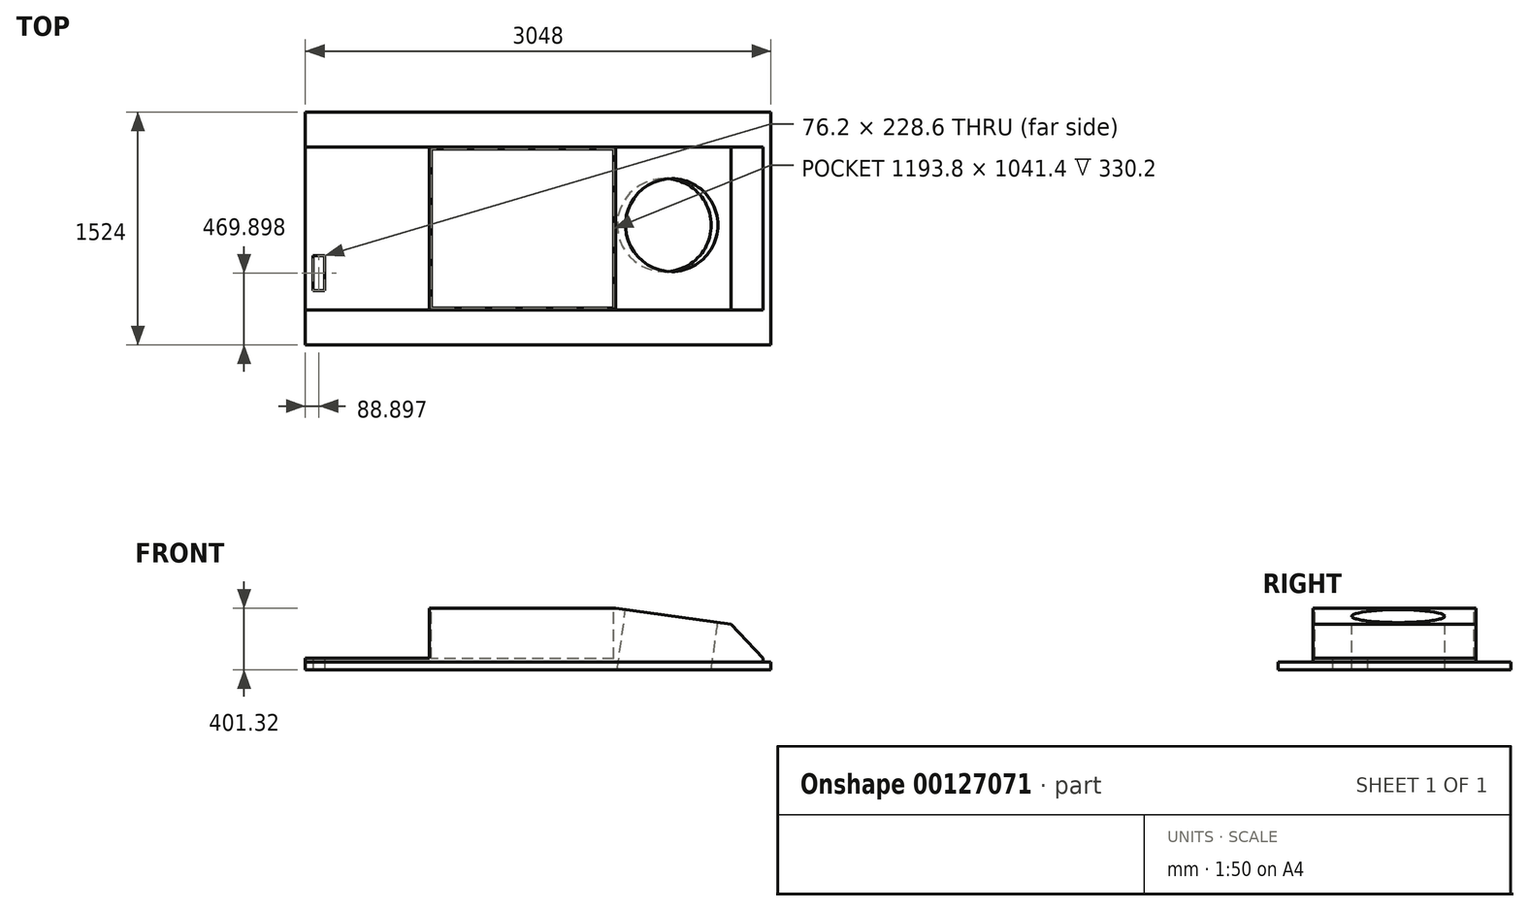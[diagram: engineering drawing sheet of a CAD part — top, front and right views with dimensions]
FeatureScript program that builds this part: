
annotation { "Feature Type Name" : "Feature", "Feature Type Description" : "" }
export const myFeature = defineFeature(function(context is Context, id is Id, definition is map)
    precondition{}
    {
        {
            var Q0;
            Q0=qCreatedBy(makeId("Top.planeOp"),FACE);
            var sketch = newSketch(context, id + "F0", { "sketchPlane" : qUnion([Q0])});
            skLineSegment(sketch, "E0.bottom", {"start": v(-1508.2, 739.4) * mm, "end": v(1539.8, 739.4) * mm});
            skLineSegment(sketch, "E0.top", {"start": v(-1508.2, -784.6) * mm, "end": v(1539.8, -784.6) * mm});
            skLineSegment(sketch, "E0.left", {"start": v(-1508.2, 739.4) * mm, "end": v(-1508.2, -784.6) * mm});
            skLineSegment(sketch, "E0.right", {"start": v(1539.8, 739.4) * mm, "end": v(1539.8, -784.6) * mm});
            skLineSegment(sketch, "E1.bottom", {"start": v(-1381.2, -429) * mm, "end": v(-1457.4, -429) * mm});
            skLineSegment(sketch, "E1.top", {"start": v(-1381.2, -200.4) * mm, "end": v(-1457.4, -200.4) * mm});
            skLineSegment(sketch, "E1.left", {"start": v(-1381.2, -429) * mm, "end": v(-1381.2, -200.4) * mm});
            skLineSegment(sketch, "E1.right", {"start": v(-1457.4, -429) * mm, "end": v(-1457.4, -200.4) * mm});
            skSolve(sketch);
        }
        {
            var Q0;
            Q0=makeQuery(id+"F0.imprint","IMPRINT",FACE,{"disambiguationData":[TD([[makeQuery(id+"F0.imprint","IMPRINT",EDGE,{"derivedFrom":sQuery(id+"F0.wireOp",EDGE,"E0.bottom")}),-1.0]])]});
            extrude(context, id + "F1", {"entities" : qUnion([Q0]), "depth" : 50.8 * mm});
        }
        {
            var Q0;
            Q0=makeQuery(id+"F1.opExtrude","CAP_FACE",FACE,{"disambiguationData":[OSD([sQuery(id+"F0.wireOp",EDGE,"E0.bottom"),sQuery(id+"F0.wireOp",EDGE,"E0.top"),sQuery(id+"F0.wireOp",EDGE,"E0.left"),sQuery(id+"F0.wireOp",EDGE,"E0.right"),sQuery(id+"F0.wireOp",EDGE,"E1.bottom"),sQuery(id+"F0.wireOp",EDGE,"E1.top"),sQuery(id+"F0.wireOp",EDGE,"E1.left"),sQuery(id+"F0.wireOp",EDGE,"E1.right")])],"isStart":false});
            var sketch = newSketch(context, id + "F2", { "sketchPlane" : qUnion([Q0])});
            skLineSegment(sketch, "E2.bottom", {"start": v(-1508.2, -556) * mm, "end": v(1489, -556) * mm});
            skLineSegment(sketch, "E2.top", {"start": v(-1508.2, 510.8) * mm, "end": v(1489, 510.8) * mm});
            skLineSegment(sketch, "E2.left", {"start": v(-1508.2, -556) * mm, "end": v(-1508.2, 510.8) * mm});
            skLineSegment(sketch, "E2.right", {"start": v(1489, -556) * mm, "end": v(1489, 510.8) * mm});
            skSolve(sketch);
        }
        {
            var Q0;
            Q0=makeQuery(id+"F2.imprint","IMPRINT",FACE,{"disambiguationData":[TD([[makeQuery(id+"F2.imprint","IMPRINT",EDGE,{"derivedFrom":sQuery(id+"F2.wireOp",EDGE,"E2.bottom")}),1.0]])]});
            extrude(context, id + "F3", {"entities" : qUnion([Q0]), "operationType" : NewBodyOperationType.ADD, "depth" : 25.4 * mm});
        }
        {
            var Q0;
            Q0=makeQuery(id+"F3.opExtrude","SWEPT_FACE",FACE,{"disambiguationData":[OSD([sQuery(id+"F2.wireOp",EDGE,"E2.top")])]});
            var sketch = newSketch(context, id + "F4", { "sketchPlane" : qUnion([Q0])});
            skLineSegment(sketch, "E3", {"start": v(-1489, 76.2) * mm, "end": v(-1278.6, 296.72) * mm});
            skLineSegment(sketch, "E4", {"start": v(-1278.6, 296.72) * mm, "end": v(-523.8, 401.32) * mm});
            skLineSegment(sketch, "E5", {"start": v(-523.8, 401.32) * mm, "end": v(695.4, 401.32) * mm});
            skLineSegment(sketch, "E6", {"start": v(695.4, 401.32) * mm, "end": v(695.4, 76.2) * mm});
            skLineSegment(sketch, "E7", {"start": v(695.4, 76.2) * mm, "end": v(-1489, 76.2) * mm});
            skSolve(sketch);
        }
        {
            var Q0;
            Q0=makeQuery(id+"F4.imprint","IMPRINT",FACE,{"disambiguationData":[TD([[makeQuery(id+"F4.imprint","IMPRINT",EDGE,{"derivedFrom":sQuery(id+"F4.wireOp",EDGE,"E3")}),-1.0]])]});
            extrude(context, id + "F5", {"entities" : qUnion([Q0]), "operationType" : NewBodyOperationType.ADD, "oppositeDirection" : true, "depth" : 1066.8 * mm});
        }
        {
            var Q0;
            Q0=makeQuery(id+"F5.opExtrude","SWEPT_FACE",FACE,{"disambiguationData":[OSD([sQuery(id+"F4.wireOp",EDGE,"E4")])]});
            var sketch = newSketch(context, id + "F6", { "sketchPlane" : qUnion([Q0])});
            skCircle(sketch, "E8", {"center": v(833.9, 0) * mm, "radius": 304.8 * mm});
            skSolve(sketch);
        }
        {
            var Q0;
            Q0 = qSketchRegion(id + "F6", true);
            extrude(context, id + "F7", {"entities" : qUnion([Q0]), "operationType" : NewBodyOperationType.REMOVE, "endBound" : BoundingType.THROUGH_ALL, "oppositeDirection" : true, "depth" : 682.47 * mm});
        }
        {
            var Q0;
            Q0=makeQuery(id+"F5.opExtrude","SWEPT_FACE",FACE,{"disambiguationData":[OSD([sQuery(id+"F4.wireOp",EDGE,"E5")])]});
            var sketch = newSketch(context, id + "F8", { "sketchPlane" : qUnion([Q0])});
            skLineSegment(sketch, "E9.0", {"start": v(511.1, -543.3) * mm, "end": v(-682.7, -543.3) * mm});
            skLineSegment(sketch, "E10.0", {"start": v(511.1, -543.3) * mm, "end": v(511.1, 498.1) * mm});
            skLineSegment(sketch, "E11.0", {"start": v(511.1, 498.1) * mm, "end": v(-682.7, 498.1) * mm});
            skLineSegment(sketch, "E12.0", {"start": v(-682.7, -543.3) * mm, "end": v(-682.7, 498.1) * mm});
            skSolve(sketch);
        }
        {
            var Q0;
            Q0 = qSketchRegion(id + "F8", true);
            var Q1;
            Q1=makeQuery(id+"F1.opExtrude","SWEPT_BODY",BODY,{"disambiguationData":[OSD([sQuery(id+"F0.wireOp",EDGE,"E0.bottom"),sQuery(id+"F0.wireOp",EDGE,"E0.top"),sQuery(id+"F0.wireOp",EDGE,"E0.left"),sQuery(id+"F0.wireOp",EDGE,"E0.right"),sQuery(id+"F0.wireOp",EDGE,"E1.bottom"),sQuery(id+"F0.wireOp",EDGE,"E1.top"),sQuery(id+"F0.wireOp",EDGE,"E1.left"),sQuery(id+"F0.wireOp",EDGE,"E1.right")])]});
            extrude(context, id + "F9", {"entities" : qUnion([Q0]), "operationType" : NewBodyOperationType.REMOVE, "oppositeDirection" : true, "endBoundEntityBody" : qUnion([Q1]), "depth" : 330.2 * mm});
        }
    });
